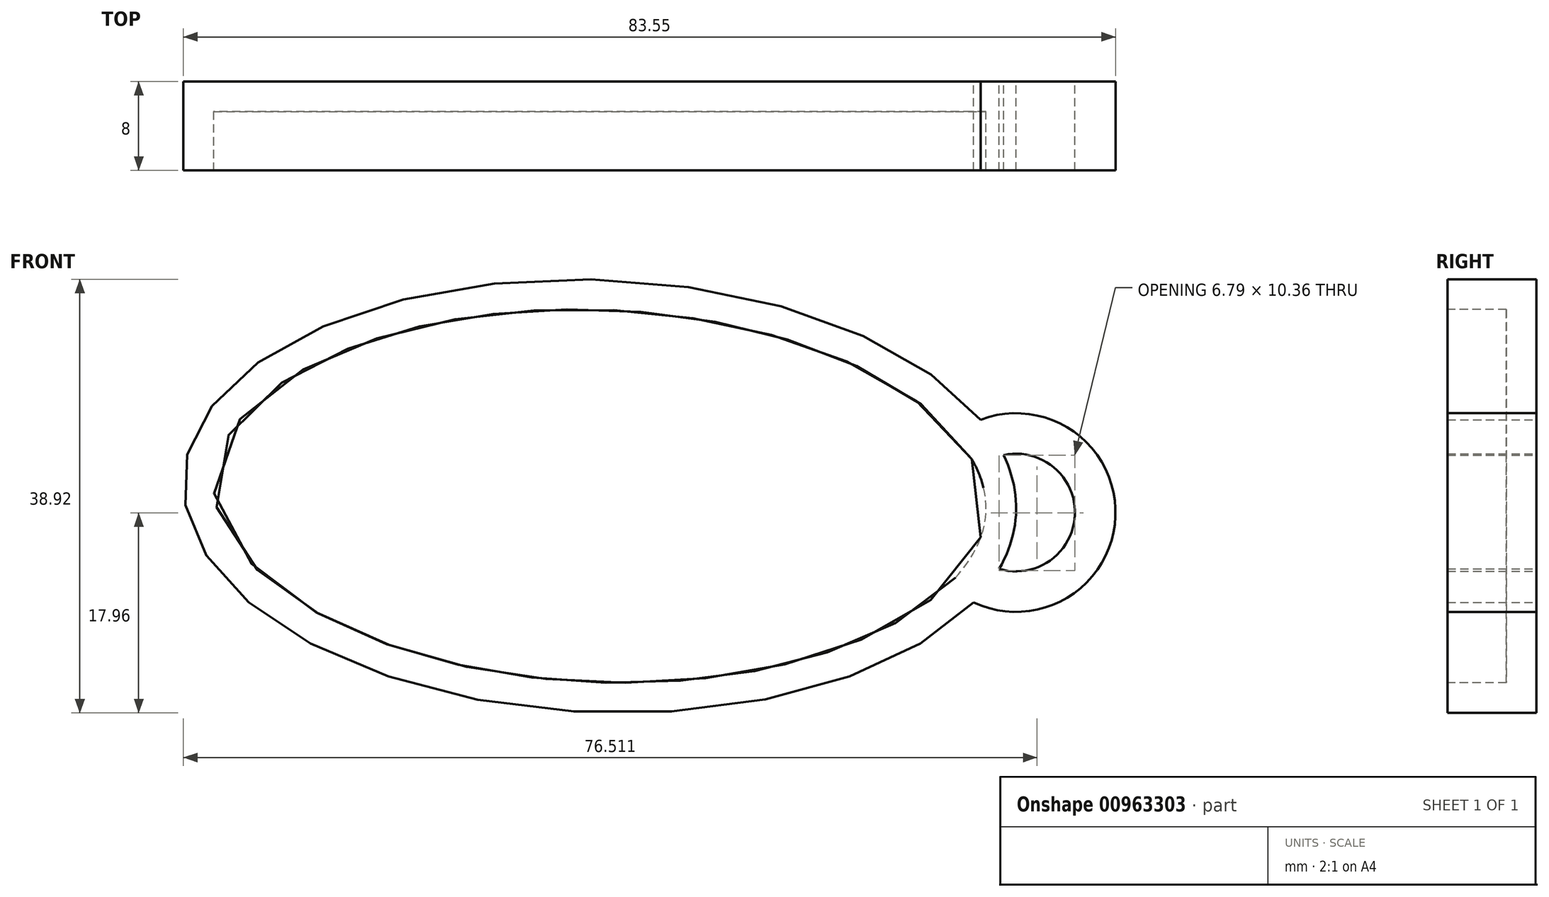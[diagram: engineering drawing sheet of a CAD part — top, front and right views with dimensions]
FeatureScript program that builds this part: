
annotation { "Feature Type Name" : "Feature", "Feature Type Description" : "" }
export const myFeature = defineFeature(function(context is Context, id is Id, definition is map)
    precondition{}
    {
        {
            var Q0;
            Q0=qCreatedBy(makeId("Front.planeOp"),FACE);
            var sketch = newSketch(context, id + "F0", { "sketchPlane" : qUnion([Q0])});
            skEllipse(sketch, "E0", {"center": v(0, 0) * mm, "majorRadius": 37.34 * mm, "minorRadius": 19.42 * mm, "majorAxis": v(1, -0.04)});
            skArc(sketch, "E1", {"start": v(33.5, -9.53) * mm, "mid": v(46.22, -1.83) * mm, "end": v(34.15, 6.86) * mm});
            skArc(sketch, "E2", {"start": v(35.8, -6.53) * mm, "mid": v(42.59, -1.68) * mm, "end": v(36.2, 3.68) * mm});
            skSolve(sketch);
        }
        {
            var Q0;
            Q0 = qSketchRegion(id + "F0", true);
            extrude(context, id + "F1", {"entities" : qUnion([Q0]), "depth" : 8 * mm, "offsetDistance" : 25.4 * mm});
        }
        {
            var Q0;
            Q0=makeQuery(id+"F1.opExtrude","CAP_FACE",FACE,{"disambiguationData":[OSD([sQuery(id+"F0.wireOp",EDGE,"E0"),sQuery(id+"F0.wireOp",EDGE,"E1"),sQuery(id+"F0.wireOp",EDGE,"E2")])],"isStart":false});
            shell(context, id + "F2", {"entities" : qUnion([Q0]), "thickness" : 2.7 * mm});
        }
    });
